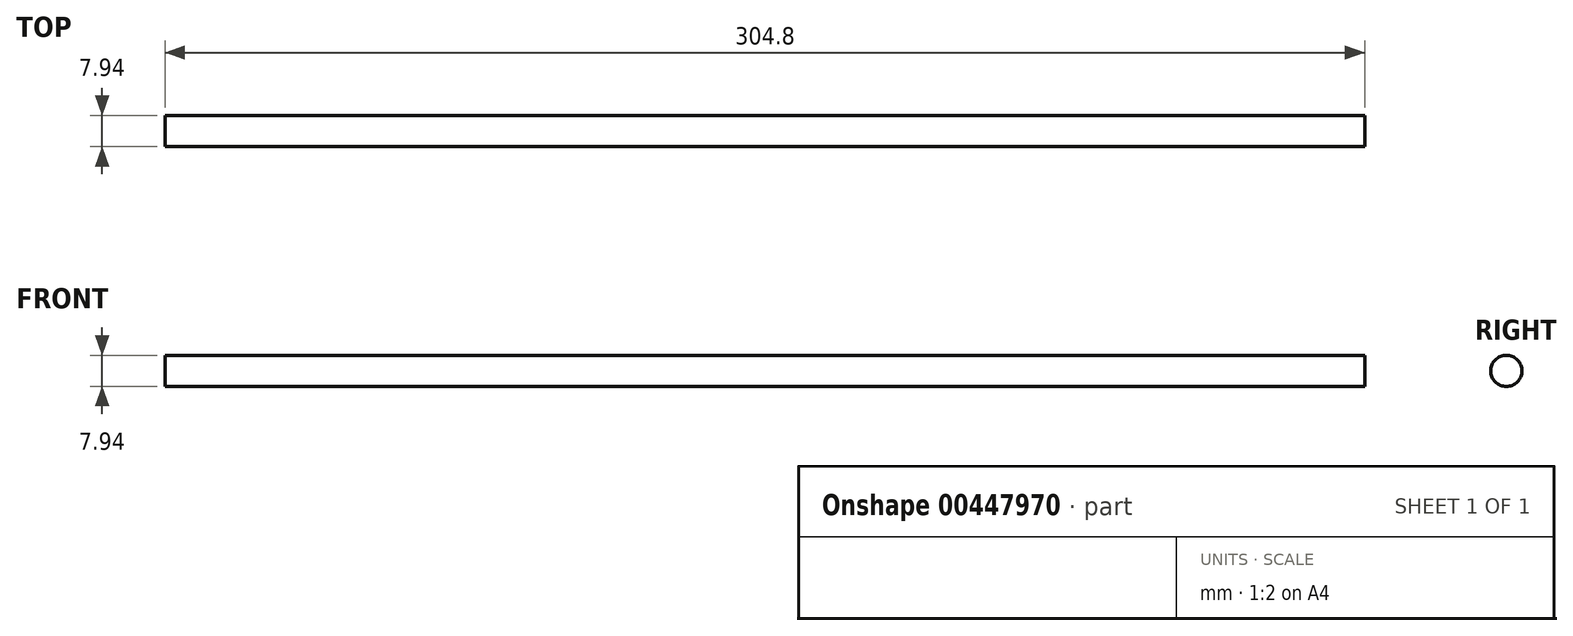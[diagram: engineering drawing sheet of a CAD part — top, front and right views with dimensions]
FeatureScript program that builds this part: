
annotation { "Feature Type Name" : "Feature", "Feature Type Description" : "" }
export const myFeature = defineFeature(function(context is Context, id is Id, definition is map)
    precondition{}
    {
        {
            var Q0;
            Q0=qCreatedBy(makeId("Right.planeOp"),FACE);
            var sketch = newSketch(context, id + "F0", { "sketchPlane" : qUnion([Q0])});
            skCircle(sketch, "E0", {"center": v(0, 0) * mm, "radius": 3.97 * mm});
            skSolve(sketch);
        }
        {
            var Q0;
            Q0=makeQuery(id+"F0.imprint","IMPRINT",FACE,{"disambiguationData":[TD([[makeQuery(id+"F0.imprint","IMPRINT",EDGE,{"derivedFrom":sQuery(id+"F0.wireOp",EDGE,"E0")}),1.0]])]});
            extrude(context, id + "F1", {"entities" : qUnion([Q0]), "depth" : 304.8 * mm});
        }
    });
